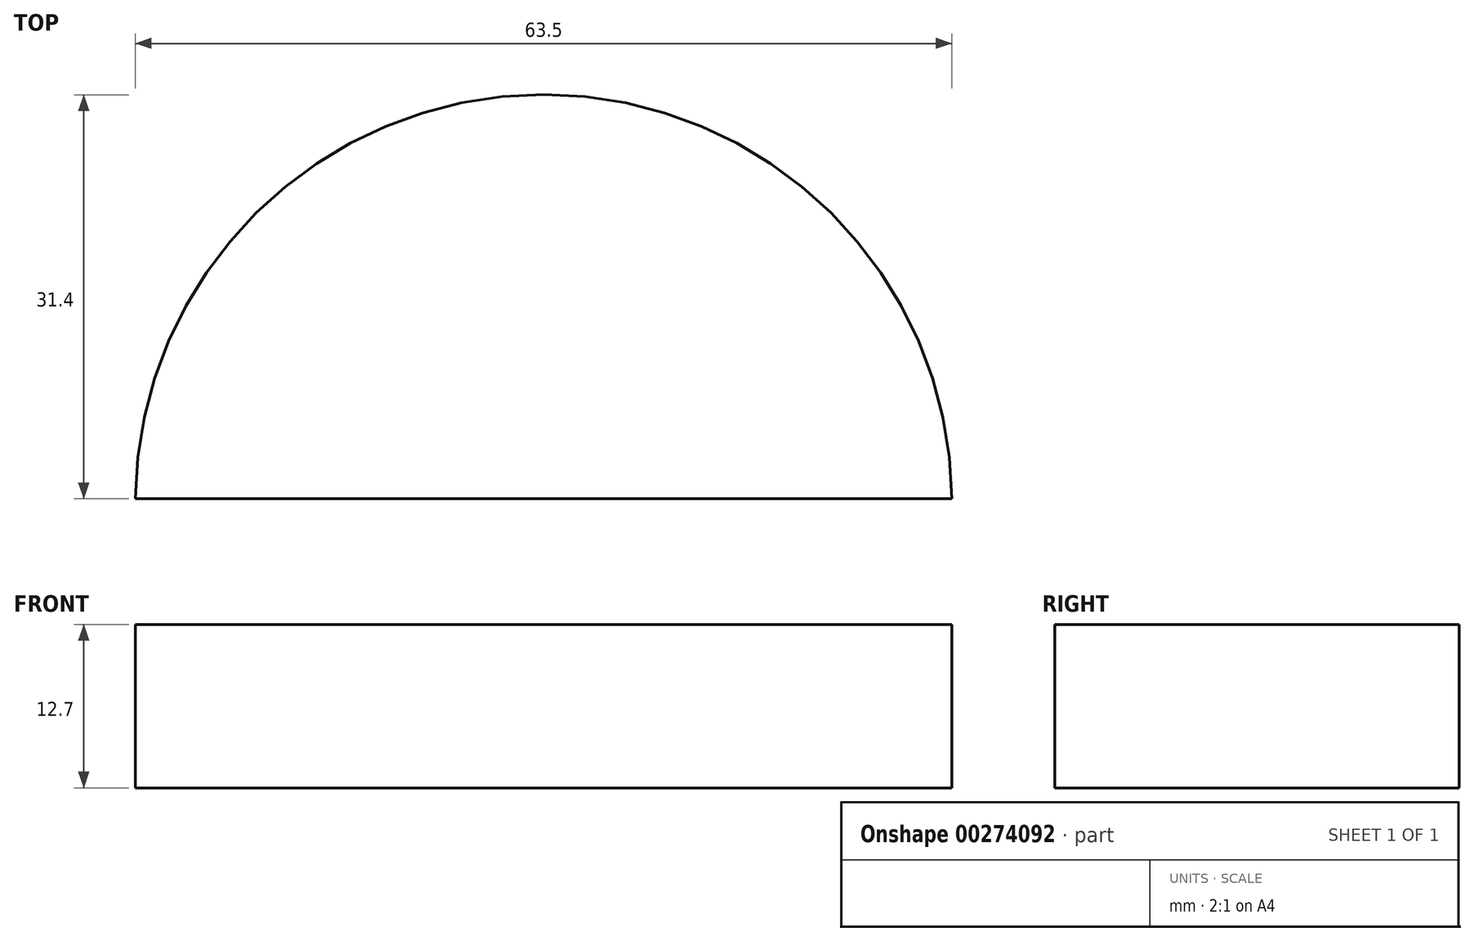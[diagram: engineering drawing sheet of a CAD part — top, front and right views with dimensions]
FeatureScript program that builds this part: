
annotation { "Feature Type Name" : "Feature", "Feature Type Description" : "" }
export const myFeature = defineFeature(function(context is Context, id is Id, definition is map)
    precondition{}
    {
        {
            var Q0;
            Q0=qCreatedBy(makeId("Top.planeOp"),FACE);
            var sketch = newSketch(context, id + "F0", { "sketchPlane" : qUnion([Q0])});
            skLineSegment(sketch, "E0", {"start": v(0, 0) * mm, "end": v(63.5, 0) * mm});
            skArc(sketch, "E1", {"start": v(63.5, 0) * mm, "mid": v(31.75, 31.4) * mm, "end": v(0, 0) * mm});
            skSolve(sketch);
        }
        {
            var Q0;
            Q0=makeQuery(id+"F0.imprint","IMPRINT",FACE,{"disambiguationData":[TD([[makeQuery(id+"F0.imprint","IMPRINT",EDGE,{"derivedFrom":sQuery(id+"F0.wireOp",EDGE,"E0")}),1.0]])]});
            extrude(context, id + "F1", {"entities" : qUnion([Q0]), "depth" : 12.7 * mm});
        }
    });
